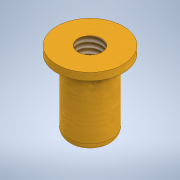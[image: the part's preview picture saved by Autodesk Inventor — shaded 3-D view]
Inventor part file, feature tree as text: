
AUTODESK INVENTOR PART (.ipt)
format: ipt  version: 2020 (Build 240168000, 168)  size: 130,560 bytes
history: native  units: mm
features: sketch x2, revolve x1, hole x1, fillet x1
ambient origin geometry x8: Origin, YZ Plane, XZ Plane, XY Plane, X Axis, Y Axis, Z Axis, Center Point
bodies: Solid1 (feature_tree)
feature tree (5):
  revolve  "Revolution1"  [1 undecoded]
  hole  "Hole1"  [1 undecoded]
  fillet  "Fillet1"  [1 undecoded]
  sketch  "Sketch1"  dims[d0=2.95mm d1=9.5mm]
  sketch  "Sketch2"  dims[d2=10.5mm d3=4.5mm d4=90.0deg d5=3.242mm d6=8.0mm d7=4.0mm d8=2.0mm d9=90.0deg d10=11.8mm d11=20.594885mm d12=1.0mm]
note: 3 required parameter values undecoded (feature->parameter linkage not recoverable at this tier; creation-order binding heuristic only, values carry confidence <= 0.55)